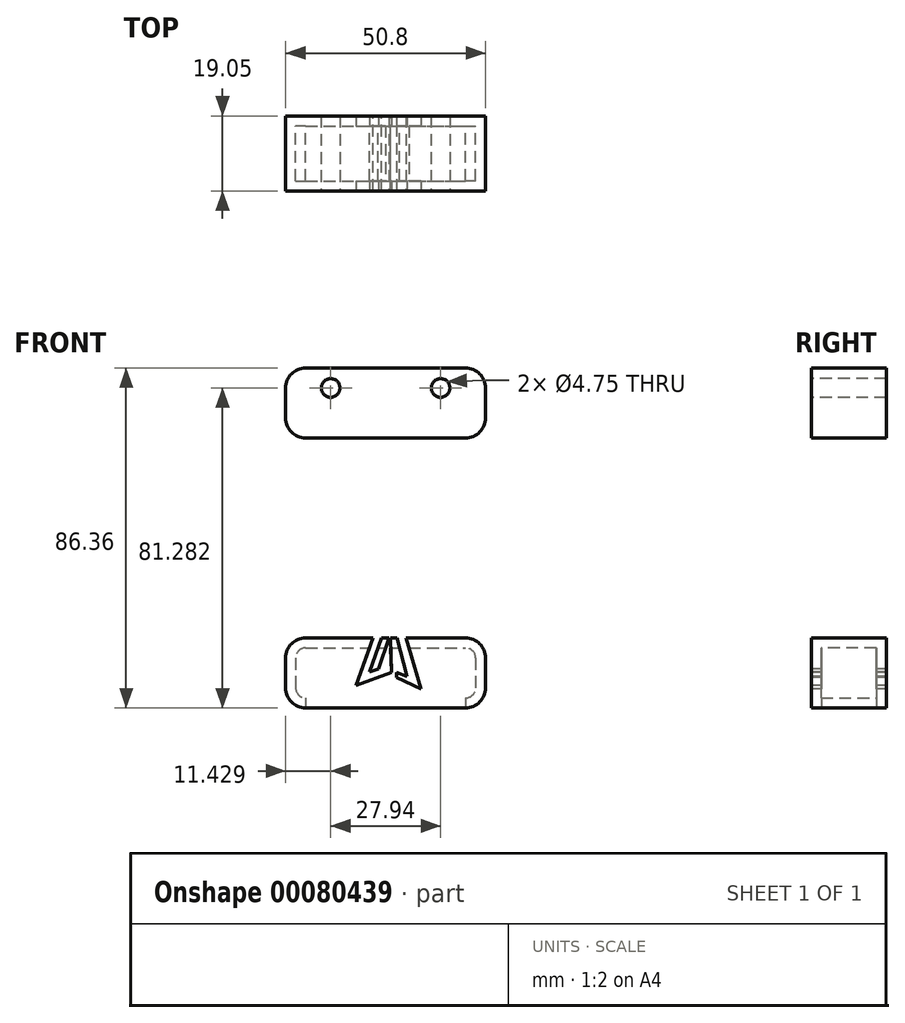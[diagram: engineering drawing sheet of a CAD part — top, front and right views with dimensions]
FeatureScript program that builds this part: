
annotation { "Feature Type Name" : "Feature", "Feature Type Description" : "" }
export const myFeature = defineFeature(function(context is Context, id is Id, definition is map)
    precondition{}
    {
        {
            var Q0;
            Q0=qCreatedBy(makeId("Front.planeOp"),FACE);
            var sketch = newSketch(context, id + "F0", { "sketchPlane" : qUnion([Q0])});
            skLineSegment(sketch, "E0.bottom", {"start": v(-34.35, 29.33) * mm, "end": v(16.45, 29.33) * mm});
            skLineSegment(sketch, "E0.top", {"start": v(-34.35, 11.55) * mm, "end": v(16.45, 11.55) * mm});
            skLineSegment(sketch, "E0.left", {"start": v(-34.35, 29.33) * mm, "end": v(-34.35, 11.55) * mm});
            skLineSegment(sketch, "E0.right", {"start": v(16.45, 29.33) * mm, "end": v(16.45, 11.55) * mm});
            skLineSegment(sketch, "E1.bottom", {"start": v(-34.35, -39.25) * mm, "end": v(16.45, -39.25) * mm});
            skLineSegment(sketch, "E1.top", {"start": v(-34.35, -57.03) * mm, "end": v(16.45, -57.03) * mm});
            skLineSegment(sketch, "E1.left", {"start": v(-34.35, -39.25) * mm, "end": v(-34.35, -57.03) * mm});
            skLineSegment(sketch, "E1.right", {"start": v(16.45, -39.25) * mm, "end": v(16.45, -57.03) * mm});
            skLineSegment(sketch, "E2.bottom", {"start": v(-24.2, -39.25) * mm, "end": v(6.29, -39.25) * mm});
            skLineSegment(sketch, "E2.top", {"start": v(-24.2, 11.55) * mm, "end": v(6.29, 11.55) * mm});
            skLineSegment(sketch, "E2.left", {"start": v(-24.2, -39.25) * mm, "end": v(-24.2, 11.55) * mm});
            skLineSegment(sketch, "E2.right", {"start": v(6.29, -39.25) * mm, "end": v(6.29, 11.55) * mm});
            skSolve(sketch);
        }
        {
            var Q0;
            Q0=makeQuery(id+"F0.imprint","IMPRINT",FACE,{"disambiguationData":[TD([[makeQuery(id+"F0.imprint","IMPRINT",EDGE,{"derivedFrom":sQuery(id+"F0.wireOp",EDGE,"E2.bottom")}),1.0]])]});
            var Q1;
            Q1=makeQuery(id+"F0.imprint","IMPRINT",FACE,{"disambiguationData":[TD([[makeQuery(id+"F0.imprint","IMPRINT",EDGE,{"derivedFrom":sQuery(id+"F0.wireOp",EDGE,"E1.top")}),1.0]])]});
            var Q2;
            Q2=makeQuery(id+"F0.imprint","IMPRINT",FACE,{"disambiguationData":[TD([[makeQuery(id+"F0.imprint","IMPRINT",EDGE,{"derivedFrom":sQuery(id+"F0.wireOp",EDGE,"E0.bottom")}),-1.0]])]});
            extrude(context, id + "F1", {"entities" : qUnion([Q0, Q1, Q2]), "depth" : 19.05 * mm});
        }
        {
            var Q0;
            Q0=makeQuery(id+"F1.opExtrude","SWEPT_EDGE",EDGE,{"disambiguationData":[OSD([sQuery(id+"F0.wireOp",EDGE,"E0.top"),sQuery(id+"F0.wireOp",EDGE,"E0.left")])]});
            var Q1;
            Q1=makeQuery(id+"F1.opExtrude","SWEPT_EDGE",EDGE,{"disambiguationData":[OSD([sQuery(id+"F0.wireOp",EDGE,"E0.top"),sQuery(id+"F0.wireOp",EDGE,"E0.right")])]});
            var Q2;
            Q2=makeQuery(id+"F1.opExtrude","SWEPT_EDGE",EDGE,{"disambiguationData":[OSD([sQuery(id+"F0.wireOp",EDGE,"E0.bottom"),sQuery(id+"F0.wireOp",EDGE,"E0.right")])]});
            var Q3;
            Q3=makeQuery(id+"F1.opExtrude","SWEPT_EDGE",EDGE,{"disambiguationData":[OSD([sQuery(id+"F0.wireOp",EDGE,"E0.bottom"),sQuery(id+"F0.wireOp",EDGE,"E0.left")])]});
            var Q4;
            Q4=makeQuery(id+"F1.opExtrude","SWEPT_EDGE",EDGE,{"disambiguationData":[OSD([sQuery(id+"F0.wireOp",EDGE,"E1.bottom"),sQuery(id+"F0.wireOp",EDGE,"E1.left")])]});
            var Q5;
            Q5=makeQuery(id+"F1.opExtrude","SWEPT_EDGE",EDGE,{"disambiguationData":[OSD([sQuery(id+"F0.wireOp",EDGE,"E1.top"),sQuery(id+"F0.wireOp",EDGE,"E1.left")])]});
            var Q6;
            Q6=makeQuery(id+"F1.opExtrude","SWEPT_EDGE",EDGE,{"disambiguationData":[OSD([sQuery(id+"F0.wireOp",EDGE,"E1.top"),sQuery(id+"F0.wireOp",EDGE,"E1.right")])]});
            var Q7;
            Q7=makeQuery(id+"F1.opExtrude","SWEPT_EDGE",EDGE,{"disambiguationData":[OSD([sQuery(id+"F0.wireOp",EDGE,"E1.bottom"),sQuery(id+"F0.wireOp",EDGE,"E1.right")])]});
            fillet(context, id + "F2", {"entities" : qUnion([Q0, Q1, Q2, Q3, Q4, Q5, Q6, Q7]), "radius" : 5.08 * mm, "tangentPropagation" : true, "allowEdgeOverflow" : false});
        }
        {
            var Q0;
            Q0=makeQuery(id+"F1.opExtrude","CAP_FACE",FACE,{"disambiguationData":[OSD([sQuery(id+"F0.wireOp",EDGE,"E0.bottom"),sQuery(id+"F0.wireOp",EDGE,"E0.top"),sQuery(id+"F0.wireOp",EDGE,"E0.left"),sQuery(id+"F0.wireOp",EDGE,"E0.right"),sQuery(id+"F0.wireOp",EDGE,"E1.bottom"),sQuery(id+"F0.wireOp",EDGE,"E1.top"),sQuery(id+"F0.wireOp",EDGE,"E1.left"),sQuery(id+"F0.wireOp",EDGE,"E1.right"),sQuery(id+"F0.wireOp",EDGE,"E2.left"),sQuery(id+"F0.wireOp",EDGE,"E2.right")])],"isStart":false});
            var sketch = newSketch(context, id + "F3", { "sketchPlane" : qUnion([Q0])});
            skCircle(sketch, "E3", {"center": v(-22.92, 24.25) * mm, "radius": 2.37 * mm});
            skCircle(sketch, "E4.MirrorC", {"center": v(5.02, 24.25) * mm, "radius": 2.37 * mm});
            skSolve(sketch);
        }
        {
            var Q0;
            Q0=makeQuery(id+"F1.opExtrude","SWEPT_FACE",FACE,{"disambiguationData":[OSD([sQuery(id+"F0.wireOp",EDGE,"E1.top")])]});
            shell(context, id + "F4", {"entities" : qUnion([Q0]), "thickness" : 2.54 * mm});
        }
        {
            var Q0;
            Q0 = qSketchRegion(id + "F3", true);
            extrude(context, id + "F5", {"entities" : qUnion([Q0]), "operationType" : NewBodyOperationType.REMOVE, "oppositeDirection" : true, "depth" : 45.6 * mm});
        }
        {
            var Q0;
            Q0=makeQuery(id+"F1.opExtrude","CAP_FACE",FACE,{"disambiguationData":[OSD([sQuery(id+"F0.wireOp",EDGE,"E0.bottom"),sQuery(id+"F0.wireOp",EDGE,"E0.top"),sQuery(id+"F0.wireOp",EDGE,"E0.left"),sQuery(id+"F0.wireOp",EDGE,"E0.right"),sQuery(id+"F0.wireOp",EDGE,"E1.bottom"),sQuery(id+"F0.wireOp",EDGE,"E1.top"),sQuery(id+"F0.wireOp",EDGE,"E1.left"),sQuery(id+"F0.wireOp",EDGE,"E1.right"),sQuery(id+"F0.wireOp",EDGE,"E2.left"),sQuery(id+"F0.wireOp",EDGE,"E2.right")])],"isStart":false});
            var sketch = newSketch(context, id + "F6", { "sketchPlane" : qUnion([Q0])});
            skLineSegment(sketch, "E5", {"start": v(-3.04, 6.35) * mm, "end": v(-11.84, -7.3) * mm});
            skLineSegment(sketch, "E6", {"start": v(-11.84, -7.3) * mm, "end": v(-8.68, -7.3) * mm});
            skLineSegment(sketch, "E7", {"start": v(-8.68, -7.3) * mm, "end": v(-15.04, -23.82) * mm});
            skLineSegment(sketch, "E8", {"start": v(-15.04, -23.82) * mm, "end": v(-4.7, -4.55) * mm});
            skLineSegment(sketch, "E9", {"start": v(-4.7, -4.55) * mm, "end": v(-7.22, -4.55) * mm});
            skLineSegment(sketch, "E10", {"start": v(-7.22, -4.55) * mm, "end": v(-3.04, 6.35) * mm});
            skLineSegment(sketch, "E11", {"start": v(-16.41, -51.38) * mm, "end": v(-7.56, -26.22) * mm});
            skLineSegment(sketch, "E12", {"start": v(-7.56, -26.22) * mm, "end": v(0, -52.2) * mm});
            skLineSegment(sketch, "E13", {"start": v(0, -52.2) * mm, "end": v(-6.12, -49.26) * mm});
            skLineSegment(sketch, "E14", {"start": v(-6.12, -49.26) * mm, "end": v(-6.12, -48.07) * mm});
            skLineSegment(sketch, "E15", {"start": v(-6.12, -48.07) * mm, "end": v(-3.47, -49) * mm});
            skLineSegment(sketch, "E16", {"start": v(-3.47, -49) * mm, "end": v(-7.8, -32.93) * mm});
            skLineSegment(sketch, "E17", {"start": v(-16.41, -51.38) * mm, "end": v(-7.44, -48.07) * mm});
            skLineSegment(sketch, "E18", {"start": v(-7.44, -48.07) * mm, "end": v(-7.8, -38.58) * mm});
            skLineSegment(sketch, "E19", {"start": v(-7.8, -38.58) * mm, "end": v(-10.8, -47.17) * mm});
            skLineSegment(sketch, "E20", {"start": v(-10.8, -47.17) * mm, "end": v(-13.02, -47.86) * mm});
            skLineSegment(sketch, "E21", {"start": v(-13.02, -47.86) * mm, "end": v(-7.8, -32.93) * mm});
            skSolve(sketch);
        }
        {
            var Q0;
            Q0=makeQuery(id+"F6.imprint","IMPRINT",FACE,{"disambiguationData":[TD([[makeQuery(id+"F6.imprint","IMPRINT",EDGE,{"derivedFrom":sQuery(id+"F6.wireOp",EDGE,"E5")}),1.0]])]});
            extrude(context, id + "F7", {"entities" : qUnion([Q0]), "operationType" : NewBodyOperationType.REMOVE, "oppositeDirection" : true, "depth" : 16.68 * mm});
        }
        {
            var Q0;
            Q0 = qSketchRegion(id + "F6", true);
            extrude(context, id + "F8", {"entities" : qUnion([Q0]), "operationType" : NewBodyOperationType.REMOVE, "oppositeDirection" : true, "depth" : 25.4 * mm});
        }
    });
